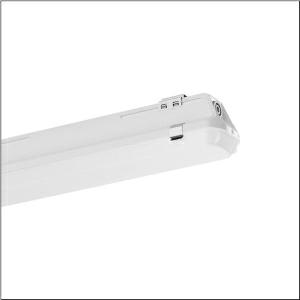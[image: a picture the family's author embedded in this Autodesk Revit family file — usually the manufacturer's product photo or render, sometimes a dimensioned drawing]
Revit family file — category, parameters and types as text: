
# Revit family: monsun_r__11_emergency_51fp207p437h3g_0ff0
name_source: partatom
category: Lighting Fixtures
units: mm (PartAtom-declared; Revit-internal decimal feet)

## family parameters
Cut with Voids When Loaded = No
Host = Face
Light Source = No
Part Type = Normal
Room Calculation Point = No
Round Connector Dimension = Use Diameter
Shared = No

## types (1)
- Monsun® 11 emergency (1 x LED, 3990 lm, 27.5 W, 4000K)
    Apparent Load = 28 VA
    CIE Flux Codes = 45 75 93 94 100
    Color Rendering = 80
    Color Temperature = 4000K
    Default Elevation = 1800 mm
    Description = Monsun® 11 emergency, damp-proof luminaire, chain hanger, primary optical cover: enclosure, of PC, light emission: direct distribution, primary light characteristic: symmetric, installation type: suspended mounting, surface-mounted, horizontal mounting, vertical mounting, LED, rated luminous flux: 3.990lm, luminous efficacy: 145lm/W, light colour: 840, colour temperature: 4000K, control gear: ECG, with terminal, 4-pole, max. 2.5mm², mains connection: 220..240V, AC, 50/60Hz, rated input power: 28W, control gear: single battery element, battery: NiCd, 4,5Ah, mains connection: 230V, luminaire housing, of glass-fibre reinforced polyester, uncoated, bright grey, incl. chain hanger, length: 1.590mm, width: 90mm, height: 88mm, clip for enclosure, of stainless steel (V2A), ceiling mounting element, of stainless steel (V2A), chain hanger, of stainless steel (V2A), protection rating (complete): IP66, insulation class (complete): insulation class I (protective earthing), certification: CE, UKCA, protection symbol: D, impact resistance: IK08, permissible operating ambient temperature: +5..+35°C, standard: EN 50419, EN 60598-2-1, EN 60598-2-22, no direct snow, no direct sun, no direct rain, for indoor or canopied outdoor use, corresponds to IFS (International Featured Standards) requirements for safety and quality in the food industry, contact your sales advisor before using the luminaires in applications with unclear chemical exposure, large temperature fluctuations or condensation-forming humidity, LABS conformity tested according to VDMA 24364:2018-05, packaging unit: 1 piece
    Height = 89 mm
    Lamp = 1 x LED
    Lamp Light Flux = 3990 lm
    Lamp Power = 27.5 W
    Lamp count = 1
    Length = 1590 mm
    Luminous efficacy = 145 lm/W
    Manufacturer = Siteco
    ModVariant = No
    Model = 51FP207P437H3G
    Mounting Place = Ceiling
    Mounting Type = Surface mounted
    Number of Poles = 1
    OnlyDefault = Yes
    Power Factor = 1
    Product Name = Monsun® 11 emergency
    Product group = damp-proof luminaire
    ProductGroupID = 300
    Protection Class = Protection class I
    Protection Degree = IP 66
    RLX_Detail_Level = 1
    RLX_Emergency_Light_Flux = 0 lm
    RLX_Emergency_Type = 0
    RLX_Emergency_Type_DB = No
    RlxData = <blob elided: 89073 chars, md5=e0b2e7cd>
    Socket = socket
    Standby Power = 0 W
    System Light Flux = 3990 lm
    System Power = 28 W
    Type Comments = Product without accessories
    Type Image = l_1319650.jpg
    URL = http://relux.com
    VarID = ---
    Voltage = 0 V
    Weight = 0.00 kg
    Width = 90 mm

## geometry (parser evidence)
native form markers: Blend x4, Sweep x12
no freeform markers — native parametric forms only
